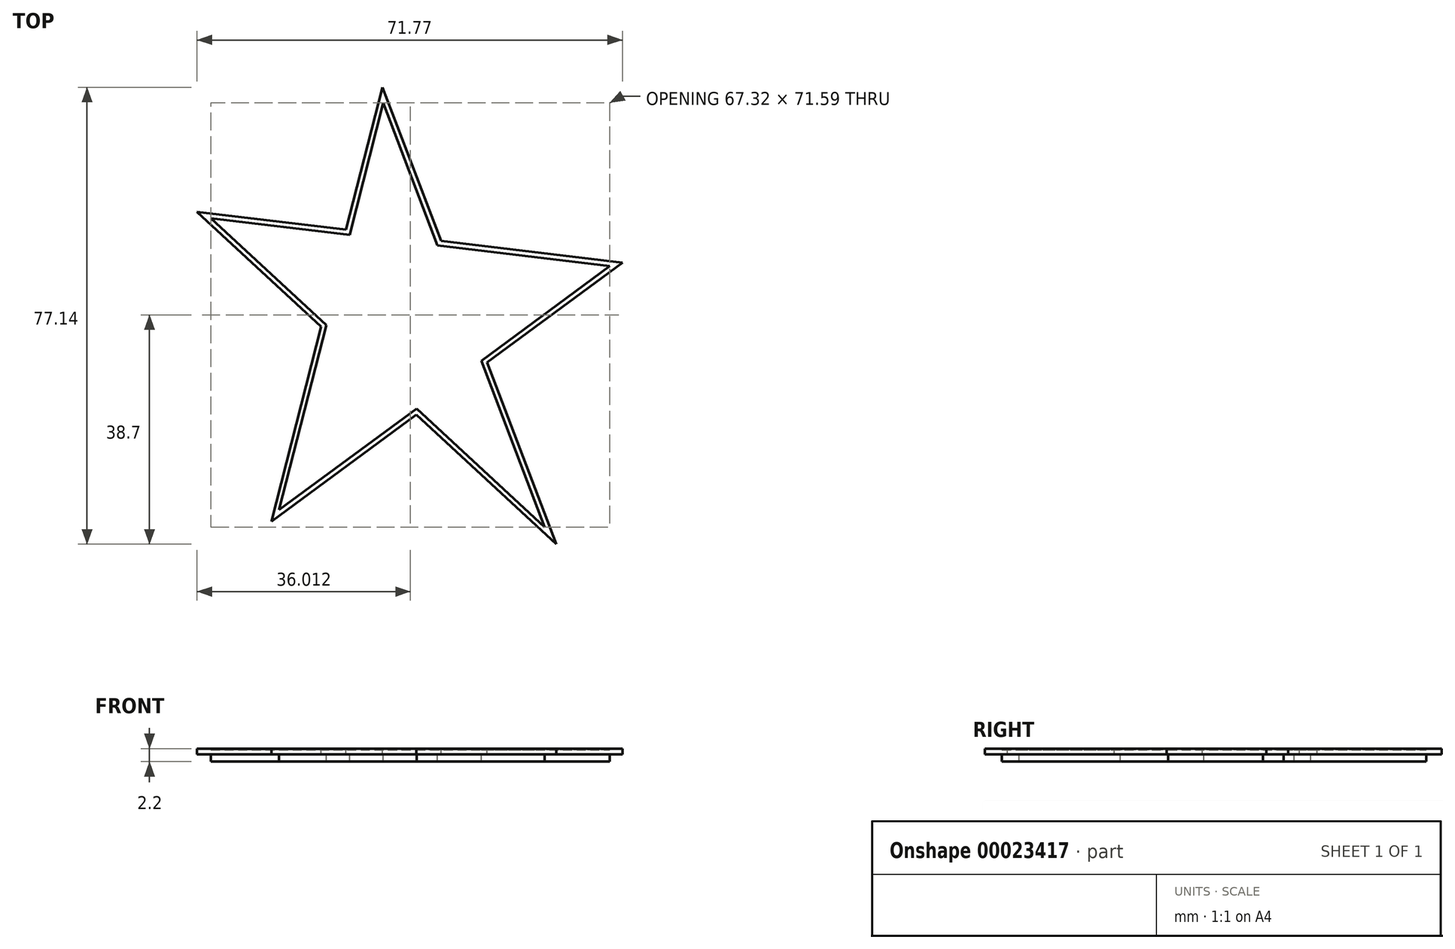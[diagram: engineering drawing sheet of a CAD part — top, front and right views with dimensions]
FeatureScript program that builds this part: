
annotation { "Feature Type Name" : "Feature", "Feature Type Description" : "" }
export const myFeature = defineFeature(function(context is Context, id is Id, definition is map)
    precondition{}
    {
        {
            var Q0;
            Q0=qCreatedBy(makeId("Top.planeOp"),FACE);
            var sketch = newSketch(context, id + "F0", { "sketchPlane" : qUnion([Q0])});
            skLineSegment(sketch, "E0", {"start": v(-7.63, 46.49) * mm, "end": v(-26.4, -26.84) * mm});
            skLineSegment(sketch, "E1", {"start": v(-26.4, -26.84) * mm, "end": v(32.85, 16.86) * mm});
            skLineSegment(sketch, "E2", {"start": v(32.85, 16.86) * mm, "end": v(-38.92, 25.46) * mm});
            skLineSegment(sketch, "E3", {"start": v(-38.92, 25.46) * mm, "end": v(21.7, -30.65) * mm});
            skLineSegment(sketch, "E4", {"start": v(21.7, -30.65) * mm, "end": v(-7.63, 46.49) * mm});
            skSolve(sketch);
        }
        {
            var Q0;
            {var subQ1=sQuery(id+"F0.wireOp",EDGE,"E2");var subQ7=sQuery(id+"F0.wireOp",EDGE,"E0");var subQ9=makeQuery(id+"F0.imprint","INTERSECT",VERTEX,{"derivedFrom":[subQ7,subQ1]});Q0=makeQuery(id+"F0.imprint","IMPRINT",FACE,{"disambiguationData":[TD([[makeQuery(id+"F0.imprint","IMPRINT",EDGE,{"disambiguationData":[TD([[subQ9,-1.0]])],"derivedFrom":subQ7}),1.0]])]});}
            var Q1;
            {var subQ0=sQuery(id+"F0.wireOp",EDGE,"E4");var subQ3=sQuery(id+"F0.wireOp",EDGE,"E0");var subQ4=makeQuery(id+"F0.imprint","INTERSECT",VERTEX,{"derivedFrom":[subQ3,subQ0]});Q1=makeQuery(id+"F0.imprint","IMPRINT",FACE,{"disambiguationData":[TD([[makeQuery(id+"F0.imprint","IMPRINT",EDGE,{"disambiguationData":[TD([[subQ4,-1.0]])],"derivedFrom":subQ3}),1.0]])]});}
            var Q2;
            {var subQ1=sQuery(id+"F0.wireOp",EDGE,"E0");var subQ3=sQuery(id+"F0.wireOp",EDGE,"E2");var subQ5=makeQuery(id+"F0.imprint","INTERSECT",VERTEX,{"derivedFrom":[subQ1,subQ3]});Q2=makeQuery(id+"F0.imprint","IMPRINT",FACE,{"disambiguationData":[TD([[makeQuery(id+"F0.imprint","IMPRINT",EDGE,{"disambiguationData":[TD([[subQ5,-1.0]])],"derivedFrom":subQ1}),-1.0]])]});}
            var Q3;
            {var subQ1=sQuery(id+"F0.wireOp",EDGE,"E1");var subQ3=sQuery(id+"F0.wireOp",EDGE,"E0");var subQ5=makeQuery(id+"F0.imprint","INTERSECT",VERTEX,{"derivedFrom":[subQ3,subQ1]});Q3=makeQuery(id+"F0.imprint","IMPRINT",FACE,{"disambiguationData":[TD([[makeQuery(id+"F0.imprint","IMPRINT",EDGE,{"disambiguationData":[TD([[subQ5,1.0]])],"derivedFrom":subQ3}),1.0]])]});}
            var Q4;
            {var subQ1=sQuery(id+"F0.wireOp",EDGE,"E1");var subQ3=sQuery(id+"F0.wireOp",EDGE,"E3");var subQ5=makeQuery(id+"F0.imprint","INTERSECT",VERTEX,{"derivedFrom":[subQ1,subQ3]});Q4=makeQuery(id+"F0.imprint","IMPRINT",FACE,{"disambiguationData":[TD([[makeQuery(id+"F0.imprint","IMPRINT",EDGE,{"disambiguationData":[TD([[subQ5,-1.0]])],"derivedFrom":subQ1}),-1.0]])]});}
            var Q5;
            {var subQ1=sQuery(id+"F0.wireOp",EDGE,"E2");var subQ3=sQuery(id+"F0.wireOp",EDGE,"E1");var subQ5=makeQuery(id+"F0.imprint","INTERSECT",VERTEX,{"derivedFrom":[subQ3,subQ1]});Q5=makeQuery(id+"F0.imprint","IMPRINT",FACE,{"disambiguationData":[TD([[makeQuery(id+"F0.imprint","IMPRINT",EDGE,{"disambiguationData":[TD([[subQ5,1.0]])],"derivedFrom":subQ3}),1.0]])]});}
            extrude(context, id + "F1", {"entities" : qUnion([Q0, Q1, Q2, Q3, Q4, Q5]), "oppositeDirection" : true, "depth" : 1 * mm});
        }
        {
            var Q0;
            Q0=makeQuery(id+"F1.opExtrude","CAP_FACE",FACE,{"disambiguationData":[OSD([sQuery(id+"F0.wireOp",EDGE,"E0"),sQuery(id+"F0.wireOp",EDGE,"E1"),sQuery(id+"F0.wireOp",EDGE,"E2"),sQuery(id+"F0.wireOp",EDGE,"E3"),sQuery(id+"F0.wireOp",EDGE,"E4")])],"isStart":true});
            shell(context, id + "F2", {"entities" : qUnion([Q0]), "thickness" : .8 * mm});
        }
        {
            var Q0;
            Q0=makeQuery(id+"F2.opShell","OFFSET_FACE",FACE,{"disambiguationData":[OSD([sQuery(id+"F0.wireOp",EDGE,"E0"),sQuery(id+"F0.wireOp",EDGE,"E1"),sQuery(id+"F0.wireOp",EDGE,"E2"),sQuery(id+"F0.wireOp",EDGE,"E3"),sQuery(id+"F0.wireOp",EDGE,"E4")])]});
            extrude(context, id + "F3", {"entities" : qUnion([Q0]), "operationType" : NewBodyOperationType.ADD, "oppositeDirection" : true, "depth" : 2 * mm});
        }
    });
